# Revit family: ITK_Патч-панель_10-дюймовое крепление_1U_Неэкранированная
name_source: partatom
category: Обобщенные модели
units: mm (PartAtom-declared; Revit-internal decimal feet)

## family parameters
Всегда вертикально = Да
Может служить основой для арматурных стержней = Нет
На основе рабочей плоскости = Нет
Общий = Нет
При загрузке вырезать с полостями = Нет
Размер круглого соединителя = Использовать диаметр
Тип детали = Нормальный
Точка расчета площади = Нет

## types (2) — shared parameters
ADSK_URL страницы изделия = https://www.itk-group.ru
ADSK_Версия Revit = 2019
ADSK_Версия семейства = 1.0
ADSK_Группирование = I. ЩИТЫ И ПУЛЬТЫ
ADSK_Единица измерения = шт
ADSK_Завод-изготовитель = IEK
ADSK_Масса = 0.45
ADSK_Материал наименование = Металл и АБС-пластик
ADSK_Наименование = ITK 1U патч-панель кат.5E UTP 12 портов 10" Dual IDC
IEK_URL = https://www.itk-group.ru
IEK_Описание = Двойная понятная маркировка IDC-модулей и портов.
Расширенный частотный диапазон работы.
Увеличенное количество циклов включения-отключения.
Совместимы со всеми 10" шкафами и стойками ITK.
Соответствие международным стандартам и ГОСТ Р.
KSI_CMa_Строительные материалы = 10.03.02.06
KSI_CPr_Строительные изделия = 27.12.31.61.1.04.09-1090
URL = https://www.iek.ru
Высота = 45 мм
Глубина = 30 мм
Изготовитель = ITK
Материал = Окраска - RAL 9005
Ширина = 254 мм

## per-type parameters (varying)
| type | IEK_Цена за единицу |
| PP12-1UC5EU-D05-10 | 972.95 |
| PP12-1UC06U-D05-10 | 1195.7 |

note: column(s) folded — value = type name in every type: ADSK_Код изделия
